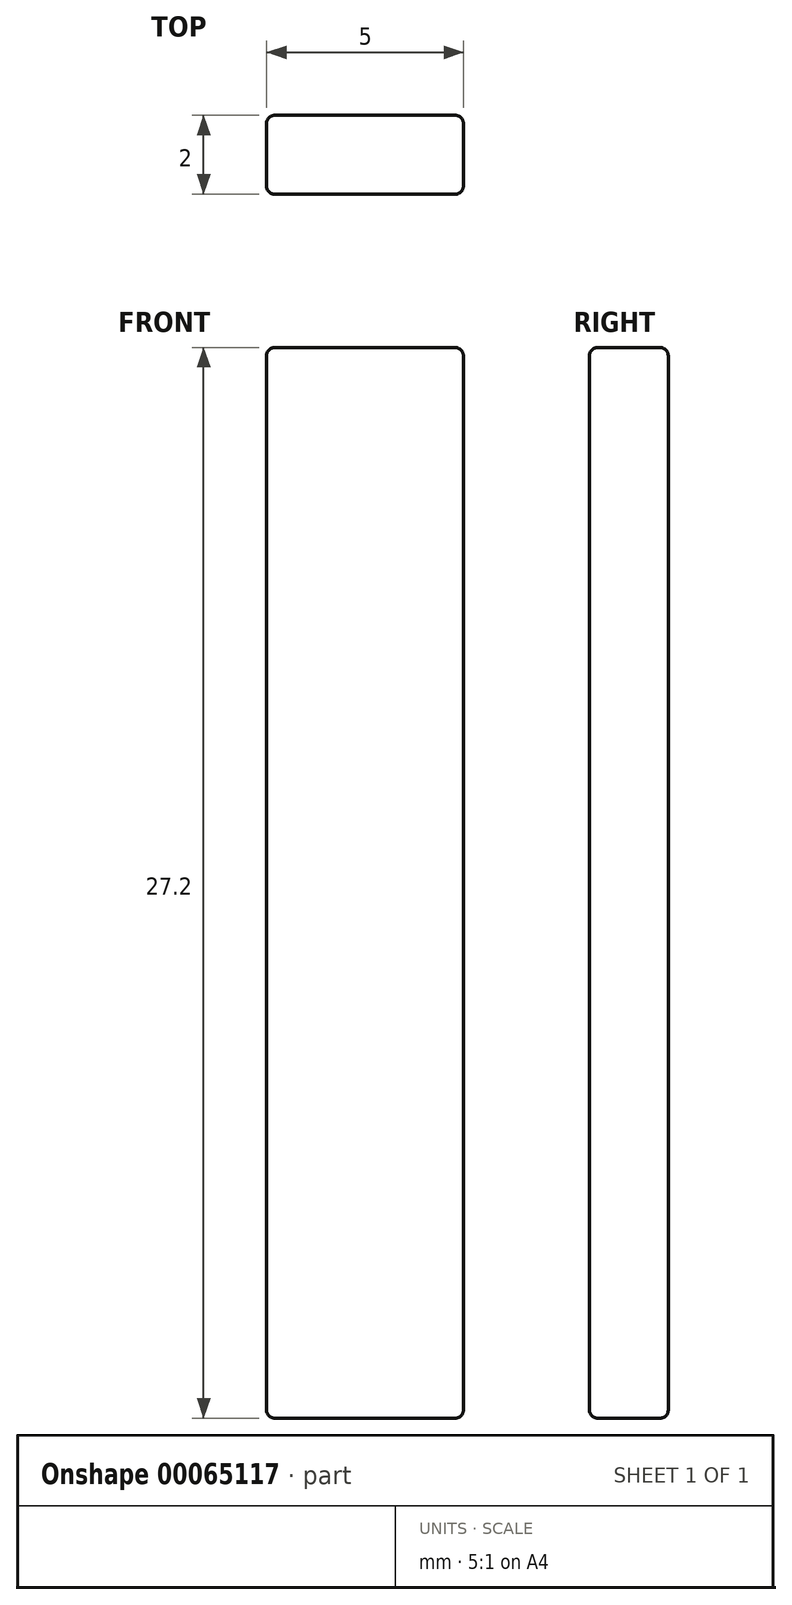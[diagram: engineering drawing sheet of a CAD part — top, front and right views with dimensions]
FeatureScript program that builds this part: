
annotation { "Feature Type Name" : "Feature", "Feature Type Description" : "" }
export const myFeature = defineFeature(function(context is Context, id is Id, definition is map)
    precondition{}
    {
        {
            var Q0;
            Q0=qCreatedBy(makeId("Top.planeOp"),FACE);
            var sketch = newSketch(context, id + "F0", { "sketchPlane" : qUnion([Q0])});
            skLineSegment(sketch, "E0", {"start": v(22.5, 2.5) * mm, "end": v(23.5, 15.5) * mm});
            skLineSegment(sketch, "E1", {"start": v(23.5, 15.5) * mm, "end": v(19, 26) * mm});
            skLineSegment(sketch, "E2", {"start": v(19, 26) * mm, "end": v(25.53, 26) * mm});
            skLineSegment(sketch, "E3", {"start": v(25.53, 26) * mm, "end": v(29.6, 16.5) * mm});
            skLineSegment(sketch, "E4", {"start": v(29.6, 16.5) * mm, "end": v(27.86, -6) * mm});
            skLineSegment(sketch, "E5", {"start": v(27.86, -6) * mm, "end": v(-27, -6) * mm});
            skLineSegment(sketch, "E6", {"start": v(-27, -6) * mm, "end": v(-36.5, 29.01) * mm});
            skLineSegment(sketch, "E7", {"start": v(-36.5, 29.01) * mm, "end": v(-36.5, 32) * mm});
            skLineSegment(sketch, "E8", {"start": v(-36.5, 32) * mm, "end": v(-18.5, 32) * mm});
            skLineSegment(sketch, "E9", {"start": v(-18.5, 32) * mm, "end": v(-18.5, 26) * mm});
            skLineSegment(sketch, "E10", {"start": v(-18.5, 26) * mm, "end": v(-23.5, 26) * mm});
            skLineSegment(sketch, "E11", {"start": v(-23.5, 26) * mm, "end": v(-26.7, 15.8) * mm});
            skLineSegment(sketch, "E12", {"start": v(-26.7, 15.8) * mm, "end": v(-23.5, 4) * mm});
            skLineSegment(sketch, "E13", {"start": v(-23.5, 4) * mm, "end": v(-19.5, 0) * mm});
            skLineSegment(sketch, "E14", {"start": v(-19.5, 0) * mm, "end": v(19.5, 0) * mm});
            skLineSegment(sketch, "E15", {"start": v(19.5, 0) * mm, "end": v(22.5, 2.5) * mm});
            skSolve(sketch);
        }
        {
            var Q0;
            Q0=qCreatedBy(makeId("Top.planeOp"),FACE);
            var sketch = newSketch(context, id + "F1", { "sketchPlane" : qUnion([Q0])});
            skLineSegment(sketch, "E16", {"start": v(22.8, 20.92) * mm, "end": v(24.65, 21.7) * mm, "construction": true});
            skLineSegment(sketch, "E17", {"start": v(24.65, 21.7) * mm, "end": v(26.62, 17.11) * mm, "construction": true});
            skLineSegment(sketch, "E18", {"start": v(26.62, 17.11) * mm, "end": v(24.78, 16.32) * mm, "construction": true});
            skLineSegment(sketch, "E19", {"start": v(24.78, 16.32) * mm, "end": v(22.8, 20.92) * mm, "construction": true});
            skLineSegment(sketch, "E20", {"start": v(-23.4, -1.5) * mm, "end": v(-18.4, -1.5) * mm});
            skLineSegment(sketch, "E21", {"start": v(-18.4, -1.5) * mm, "end": v(-18.4, -3.5) * mm});
            skLineSegment(sketch, "E22", {"start": v(-18.4, -3.5) * mm, "end": v(-23.4, -3.5) * mm});
            skLineSegment(sketch, "E23", {"start": v(-23.4, -3.5) * mm, "end": v(-23.4, -1.5) * mm});
            skLineSegment(sketch, "E24", {"start": v(-33.25, 26.58) * mm, "end": v(-31.32, 27.1) * mm, "construction": true});
            skLineSegment(sketch, "E25", {"start": v(-31.32, 27.1) * mm, "end": v(-30.01, 22.28) * mm, "construction": true});
            skLineSegment(sketch, "E26", {"start": v(-30.01, 22.28) * mm, "end": v(-31.94, 21.75) * mm, "construction": true});
            skLineSegment(sketch, "E27", {"start": v(-31.94, 21.75) * mm, "end": v(-33.25, 26.58) * mm, "construction": true});
            skLineSegment(sketch, "E28", {"start": v(-32.28, 26.84) * mm, "end": v(-30.98, 22.02) * mm, "construction": true});
            skLineSegment(sketch, "E29", {"start": v(-23.4, -2.5) * mm, "end": v(-18.4, -2.5) * mm, "construction": true});
            skLineSegment(sketch, "E30", {"start": v(25.7, 16.72) * mm, "end": v(23.73, 21.31) * mm, "construction": true});
            skLineSegment(sketch, "E31", {"start": v(-23.4, -3.5) * mm, "end": v(-27, -6) * mm, "construction": true});
            skLineSegment(sketch, "E32", {"start": v(-33.25, 26.58) * mm, "end": v(-36.5, 29.01) * mm, "construction": true});
            skLineSegment(sketch, "E33", {"start": v(24.65, 21.7) * mm, "end": v(25.53, 26) * mm, "construction": true});
            skSolve(sketch);
        }
        {
            var Q0;
            Q0=qSketchRegion(id+"F1",true);
            extrude(context, id + "F2", {"entities" : qUnion([Q0]), "depth" : 13.6 * mm});
        }
        {
            var Q0;
            Q0=makeQuery(id+"F2.opExtrude","SWEPT_BODY",BODY,{"disambiguationData":[OSD([sQuery(id+"F1.wireOp",EDGE,"E20"),sQuery(id+"F1.wireOp",EDGE,"E21"),sQuery(id+"F1.wireOp",EDGE,"E22"),sQuery(id+"F1.wireOp",EDGE,"E23")])]});
            var Q1;
            Q1=qCreatedBy(makeId("Top.planeOp"),FACE);
            mirror(context, id + "F3", {"operationType" : NewBodyOperationType.ADD, "entities" : qUnion([Q0]), "mirrorPlane" : qUnion([Q1])});
        }
        {
            var Q0;
            {var subQ0=makeQuery(id+"F2.opExtrude","SWEPT_FACE",FACE,{"disambiguationData":[OSD([sQuery(id+"F1.wireOp",EDGE,"E21")])]});Q0=makeQuery(id+"F3.boolean.opBoolean","MERGE",FACE,{"derivedFrom":[subQ0,makeQuery(id+"F3.opPattern","COPY",FACE,{"derivedFrom":subQ0,"instanceName":"1"})]});}
            var Q1;
            Q1=makeQuery(id+"F2.opExtrude","CAP_FACE",FACE,{"disambiguationData":[OSD([sQuery(id+"F1.wireOp",EDGE,"E20"),sQuery(id+"F1.wireOp",EDGE,"E21"),sQuery(id+"F1.wireOp",EDGE,"E22"),sQuery(id+"F1.wireOp",EDGE,"E23")])],"isStart":false});
            var Q2;
            {var subQ0=makeQuery(id+"F2.opExtrude","SWEPT_FACE",FACE,{"disambiguationData":[OSD([sQuery(id+"F1.wireOp",EDGE,"E23")])]});Q2=makeQuery(id+"F3.boolean.opBoolean","MERGE",FACE,{"derivedFrom":[subQ0,makeQuery(id+"F3.opPattern","COPY",FACE,{"derivedFrom":subQ0,"instanceName":"1"})]});}
            var Q3;
            Q3=makeQuery(id+"F3.opPattern","COPY",FACE,{"derivedFrom":makeQuery(id+"F2.opExtrude","CAP_FACE",FACE,{"disambiguationData":[OSD([sQuery(id+"F1.wireOp",EDGE,"E20"),sQuery(id+"F1.wireOp",EDGE,"E21"),sQuery(id+"F1.wireOp",EDGE,"E22"),sQuery(id+"F1.wireOp",EDGE,"E23")])],"isStart":false}),"instanceName":"1"});
            fillet(context, id + "F4", {"entities" : qUnion([Q0, Q1, Q2, Q3]), "radius" : .2 * mm, "tangentPropagation" : true, "allowEdgeOverflow" : false});
        }
    });
